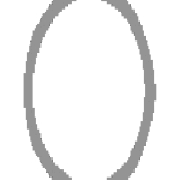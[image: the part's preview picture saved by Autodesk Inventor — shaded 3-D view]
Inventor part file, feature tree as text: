
AUTODESK INVENTOR PART (.ipt)
format: ipt  version: 2021 (Build 250183000, 183)  size: 112,640 bytes
history: native  units: in
note: dims shown in document units (in); Inventor stores cm internally (conversion verified against a paired STEP export)
features: other x4, sketch x3, plane x1
ambient origin geometry x8: Origin, YZ Plane, XZ Plane, XY Plane, X Axis, Y Axis, Z Axis, Center Point
bodies: Solid1 (feature_tree), Body (feature_tree)
feature tree (8):
  other  "Driven Length"
  other  "Frame Generator"
  other  "Start Plane"
  other  "End Plane"
  sketch  "Sketch"  dims[d2=22.0in d4=-0.0in d5=22.0in d6=0.12in d7=0.0in d8=90.0deg d9=22.0in]
  sketch  "Sketch2"  dims[d0=1.0in]
  plane  "Work Plane3"
  sketch  "Sketch3"  dims[d1=0.065in]
